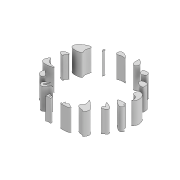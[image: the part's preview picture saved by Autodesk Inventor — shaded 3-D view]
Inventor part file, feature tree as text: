
AUTODESK INVENTOR PART (.ipt)
format: ipt  version: 2021 (Build 250183000, 183)  size: 252,928 bytes
history: native  units: in
note: dims shown in document units (in); Inventor stores cm internally (conversion verified against a paired STEP export)
features: extrude x1, mirror x1, sketch x1
ambient origin geometry x8: Origin, YZ Plane, XZ Plane, XY Plane, X Axis, Y Axis, Z Axis, Center Point
bodies: Body1 (feature_tree)
feature tree (3):
  extrude  "Extrusion2"  Depth=6.2992in TaperAngle=360.0deg
  mirror  "Mirror1"
  sketch  "Sketch1"  dims[d1=0.0773in d2=6.2992in d4=360.0deg d8=118.1102in d9=0.0in]
